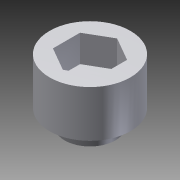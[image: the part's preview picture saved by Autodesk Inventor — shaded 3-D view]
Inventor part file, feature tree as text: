
AUTODESK INVENTOR PART (.ipt)
format: ipt  version: 2012 (Build 160160000, 160)  size: 165,376 bytes
history: native  units: mm
features: extrude x4, sketch x4, other x3, projected_geometry x3, fillet x2, reference x1
ambient origin geometry x8: Origin, YZ Plane, XZ Plane, XY Plane, X Axis, Y Axis, Z Axis, Center Point
bodies: Solid1 (feature_tree)
feature tree (17):
  other  "ServoToScrewKey.ipt"
  extrude  "Extrusion1"  TaperAngle=0.0deg  [1 undecoded]
  extrude  "Extrusion2"  Depth=2.0mm
  extrude  "Extrusion4"  Depth=1.0mm
  fillet  "Fillet1"  Radius=4.0mm
  fillet  "Fillet2"  Radius=120.0mm
  extrude  "Extrusion5"  Depth=0.5mm
  other  "Solid2::ServoToScrewKey.ipt"
  other  "TaggingFeature1"
  sketch  "Sketch2"  dims[d0=10.0mm d1=0.0mm d2=0.0mm]
  projected_geometry  "Projected Loop1"
  sketch  "Sketch3"  dims[d3=4.0mm d4=0.0mm d15=2.0mm]
  projected_geometry  "Projected Loop2"
  sketch  "Sketch8"  dims[d16=1.0mm d17=1.0mm d18=4.0mm d19=120.0mm d21=360.0deg]
  projected_geometry  "Projected Loop6"
  sketch  "Sketch9"  dims[d23=10.0mm d24=0.0mm d25=0.5mm d26=0.5mm d27=10.0mm d28=0.0mm]
  reference  "Reference1"
note: 1 required parameter value undecoded (feature->parameter linkage not recoverable at this tier; creation-order binding heuristic only, values carry confidence <= 0.55)
